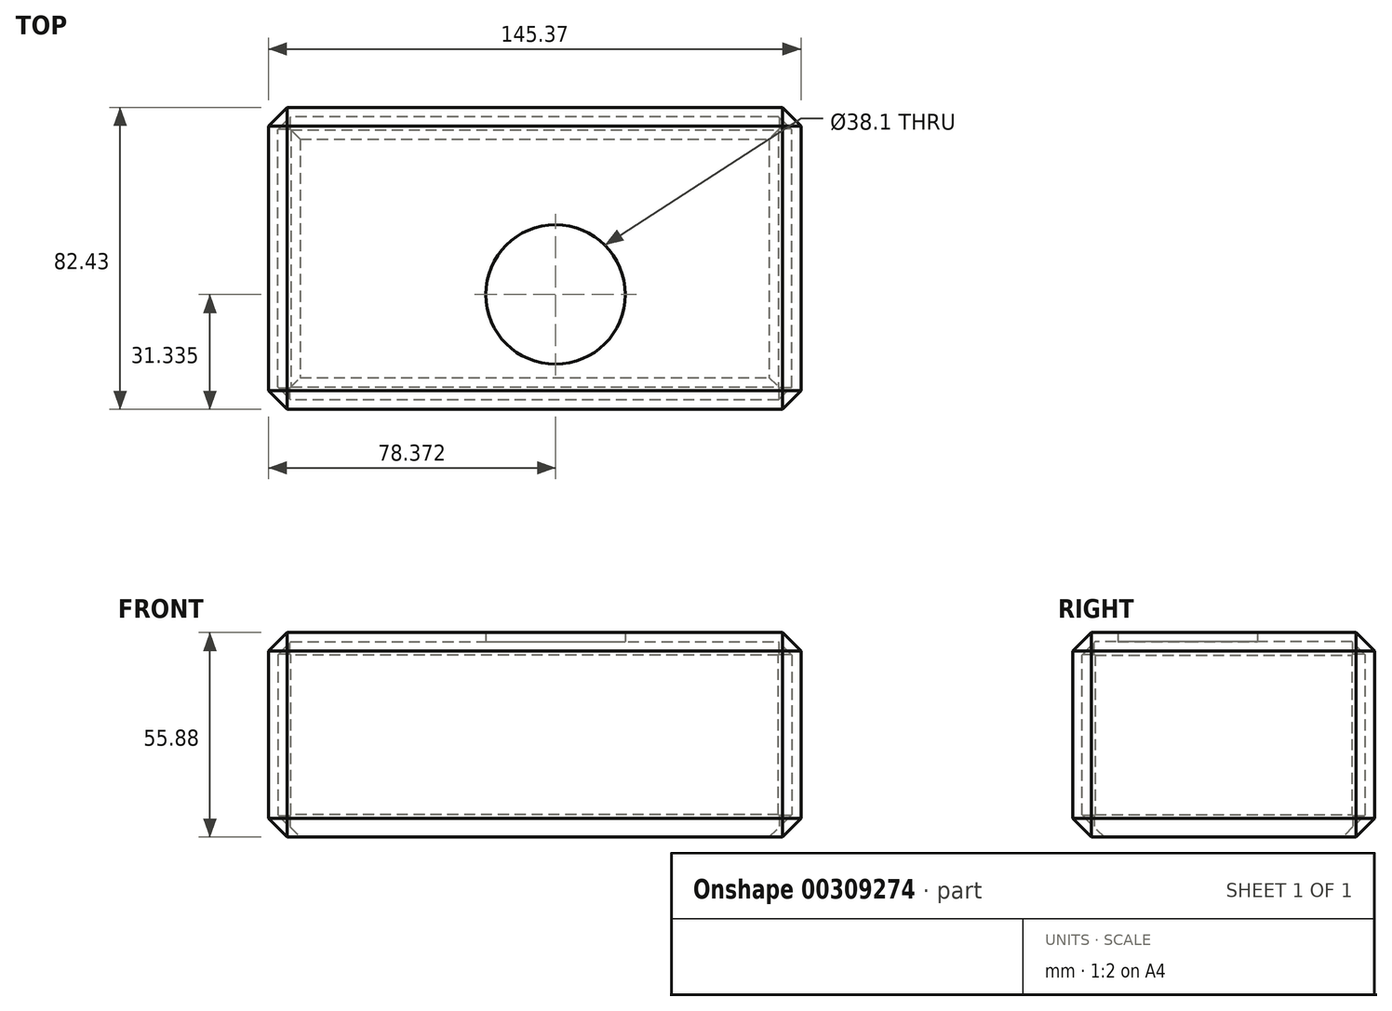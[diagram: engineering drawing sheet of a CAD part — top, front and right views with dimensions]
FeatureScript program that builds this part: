
annotation { "Feature Type Name" : "Feature", "Feature Type Description" : "" }
export const myFeature = defineFeature(function(context is Context, id is Id, definition is map)
    precondition{}
    {
        {
            var Q0;
            Q0=qCreatedBy(makeId("Top.planeOp"),FACE);
            var sketch = newSketch(context, id + "F0", { "sketchPlane" : qUnion([Q0])});
            skLineSegment(sketch, "E0.bottom", {"start": v(-104.47, 0) * mm, "end": v(40.9, 0) * mm});
            skLineSegment(sketch, "E0.top", {"start": v(-104.47, -82.43) * mm, "end": v(40.9, -82.43) * mm});
            skLineSegment(sketch, "E0.left", {"start": v(-104.47, 0) * mm, "end": v(-104.47, -82.43) * mm});
            skLineSegment(sketch, "E0.right", {"start": v(40.9, 0) * mm, "end": v(40.9, -82.43) * mm});
            skSolve(sketch);
        }
        {
            var Q0;
            Q0=makeQuery(id+"F0.imprint","IMPRINT",FACE,{"disambiguationData":[TD([[makeQuery(id+"F0.imprint","IMPRINT",EDGE,{"derivedFrom":sQuery(id+"F0.wireOp",EDGE,"E0.bottom")}),-1.0]])]});
            extrude(context, id + "F1", {"entities" : qUnion([Q0]), "depth" : 55.88 * mm});
        }
        {
            var Q0;
            Q0=makeQuery(id+"F1.opExtrude","CAP_EDGE",EDGE,{"disambiguationData":[OSD([sQuery(id+"F0.wireOp",EDGE,"E0.top")])],"isStart":false});
            var Q1;
            Q1=makeQuery(id+"F1.opExtrude","CAP_EDGE",EDGE,{"disambiguationData":[OSD([sQuery(id+"F0.wireOp",EDGE,"E0.right")])],"isStart":false});
            var Q2;
            Q2=makeQuery(id+"F1.opExtrude","CAP_EDGE",EDGE,{"disambiguationData":[OSD([sQuery(id+"F0.wireOp",EDGE,"E0.bottom")])],"isStart":false});
            var Q3;
            Q3=makeQuery(id+"F1.opExtrude","CAP_FACE",FACE,{"disambiguationData":[OSD([sQuery(id+"F0.wireOp",EDGE,"E0.bottom"),sQuery(id+"F0.wireOp",EDGE,"E0.top"),sQuery(id+"F0.wireOp",EDGE,"E0.left"),sQuery(id+"F0.wireOp",EDGE,"E0.right")])],"isStart":false});
            var Q4;
            Q4=makeQuery(id+"F1.opExtrude","SWEPT_FACE",FACE,{"disambiguationData":[OSD([sQuery(id+"F0.wireOp",EDGE,"E0.top")])]});
            var Q5;
            Q5=makeQuery(id+"F1.opExtrude","SWEPT_FACE",FACE,{"disambiguationData":[OSD([sQuery(id+"F0.wireOp",EDGE,"E0.right")])]});
            var Q6;
            Q6=makeQuery(id+"F1.opExtrude","SWEPT_FACE",FACE,{"disambiguationData":[OSD([sQuery(id+"F0.wireOp",EDGE,"E0.left")])]});
            var Q7;
            Q7=makeQuery(id+"F1.opExtrude","SWEPT_FACE",FACE,{"disambiguationData":[OSD([sQuery(id+"F0.wireOp",EDGE,"E0.bottom")])]});
            chamfer(context, id + "F2", {"entities" : qUnion([Q0, Q1, Q2, Q3, Q4, Q5, Q6, Q7]), "width" : 5.08 * mm, "tangentPropagation" : true});
        }
        {
            var Q0;
            Q0=makeQuery(id+"F1.opExtrude","CAP_FACE",FACE,{"disambiguationData":[OSD([sQuery(id+"F0.wireOp",EDGE,"E0.bottom"),sQuery(id+"F0.wireOp",EDGE,"E0.top"),sQuery(id+"F0.wireOp",EDGE,"E0.left"),sQuery(id+"F0.wireOp",EDGE,"E0.right")])],"isStart":true});
            shell(context, id + "F3", {"entities" : qUnion([Q0]), "thickness" : 2.54 * mm});
        }
        {
            var Q0;
            Q0=makeQuery(id+"F3.opShell","OFFSET_FACE",FACE,{"disambiguationData":[OSD([sQuery(id+"F0.wireOp",EDGE,"E0.bottom"),sQuery(id+"F0.wireOp",EDGE,"E0.top"),sQuery(id+"F0.wireOp",EDGE,"E0.left"),sQuery(id+"F0.wireOp",EDGE,"E0.right")])]});
            var sketch = newSketch(context, id + "F4", { "sketchPlane" : qUnion([Q0])});
            skCircle(sketch, "E1", {"center": v(-26.1, 51.1) * mm, "radius": 20.65 * mm});
            skSolve(sketch);
        }
        {
            var Q0;
            Q0=sQuery(id+"F4.wireOp",VERTEX,"E1.center");
            var Q1;
            Q1=makeQuery(id+"F1.opExtrude","SWEPT_BODY",BODY,{"disambiguationData":[OSD([sQuery(id+"F0.wireOp",EDGE,"E0.bottom"),sQuery(id+"F0.wireOp",EDGE,"E0.top"),sQuery(id+"F0.wireOp",EDGE,"E0.left"),sQuery(id+"F0.wireOp",EDGE,"E0.right")])]});
            hole(context, id + "F5", {"style" : HoleStyle.SIMPLE, "endStyle" : HoleEndStyle.THROUGH, "holeDiameter" : 38.1 * mm, "tappedDepth" : 12.7 * mm, "tapClearance" : 3, "locations" : qUnion([Q0]), "scope" : qUnion([Q1])});
        }
    });
